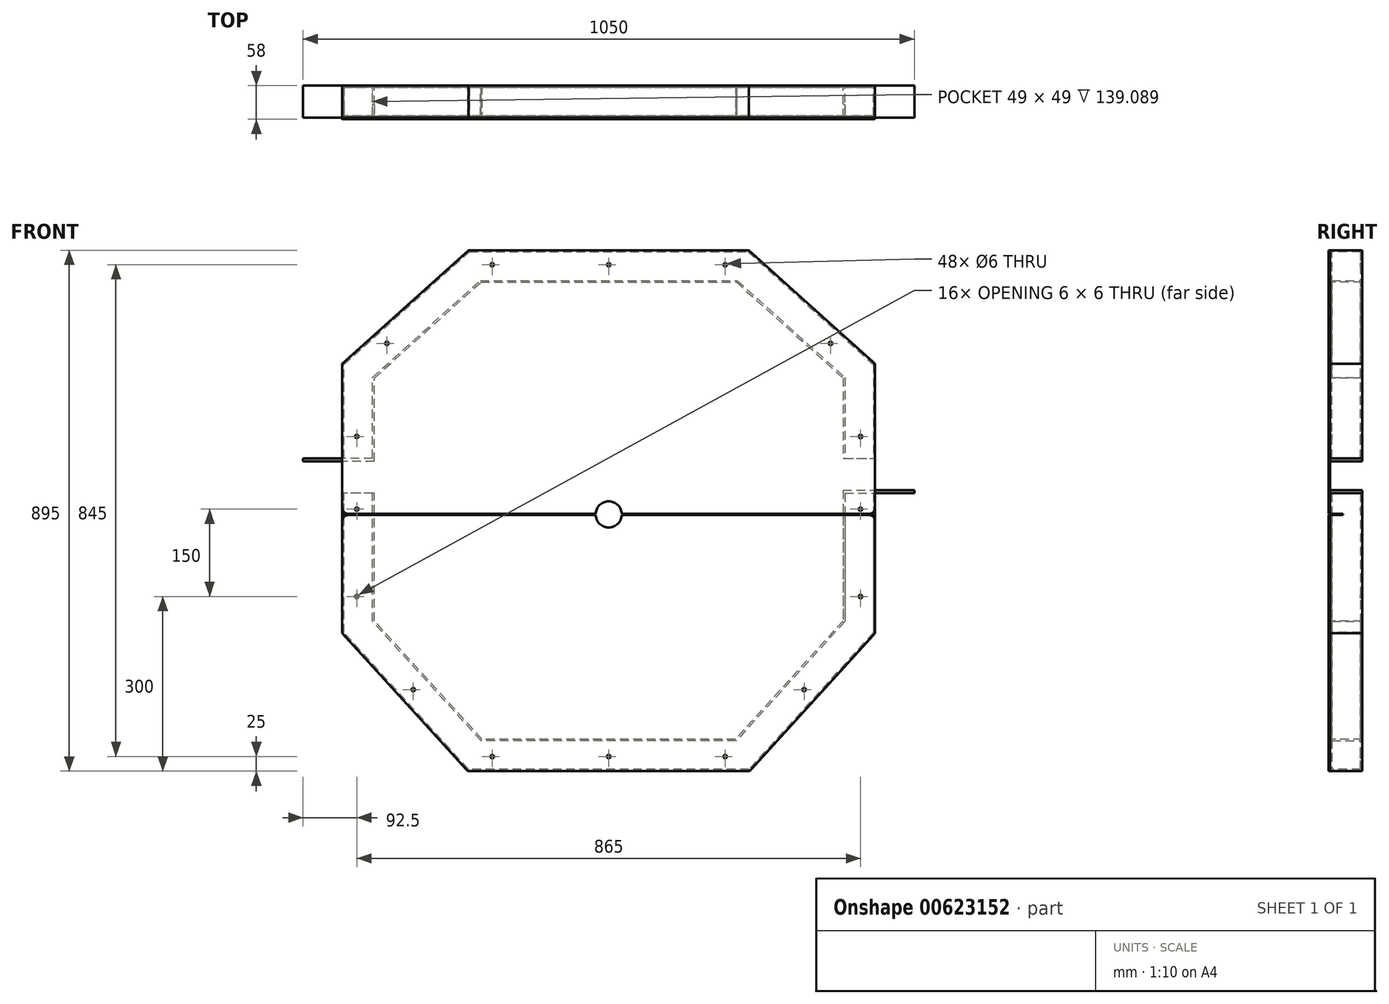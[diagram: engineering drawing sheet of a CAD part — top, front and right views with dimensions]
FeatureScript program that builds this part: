
annotation { "Feature Type Name" : "Feature", "Feature Type Description" : "" }
export const myFeature = defineFeature(function(context is Context, id is Id, definition is map)
    precondition{}
    {
        {
            var Q0;
            Q0=qCreatedBy(makeId("Front.planeOp"),FACE);
            var sketch = newSketch(context, id + "F0", { "sketchPlane" : qUnion([Q0])});
            skLineSegment(sketch, "E0", {"start": v(0, 0) * mm, "end": v(-430, 0) * mm, "construction": true});
            skLineSegment(sketch, "E1", {"start": v(0, 0) * mm, "end": v(430, 0) * mm, "construction": true});
            skPoint(sketch, "E2", {"position": v(0, -330) * mm});
            skLineSegment(sketch, "E3", {"start": v(-430, -330) * mm, "end": v(430, -330) * mm, "construction": true});
            skLineSegment(sketch, "E4", {"start": v(-430, -330) * mm, "end": v(-430, -180) * mm});
            skLineSegment(sketch, "E5", {"start": v(-430, -180) * mm, "end": v(-230, 0) * mm});
            skLineSegment(sketch, "E6", {"start": v(-230, 0) * mm, "end": v(0, 0) * mm});
            skLineSegment(sketch, "E7", {"start": v(0, 0) * mm, "end": v(230, 0) * mm});
            skLineSegment(sketch, "E8", {"start": v(430, -330) * mm, "end": v(430, -180) * mm});
            skLineSegment(sketch, "E9", {"start": v(430, -180) * mm, "end": v(230, 0) * mm});
            skSolve(sketch);
        }
        {
            var Q0;
            Q0=qCreatedBy(makeId("Top.planeOp"),FACE);
            cPlane(context, id + "F1", {"entities" : qUnion([Q0]), "cplaneType" : CPlaneType.OFFSET, "offset" : 330 * mm, "oppositeDirection" : true, "width" : 150 * mm, "height" : 150 * mm});
        }
        {
            var Q0;
            Q0=qCreatedBy(id+"F1.planeOp",FACE);
            var sketch = newSketch(context, id + "F2", { "sketchPlane" : qUnion([Q0])});
            skPoint(sketch, "E10", {"position": v(-430, 0) * mm});
            skLineSegment(sketch, "E11.bottom", {"start": v(-402.5, -27.5) * mm, "end": v(-457.5, -27.5) * mm});
            skLineSegment(sketch, "E11.top", {"start": v(-402.5, 27.5) * mm, "end": v(-457.5, 27.5) * mm});
            skLineSegment(sketch, "E11.left", {"start": v(-402.5, -27.5) * mm, "end": v(-402.5, 27.5) * mm});
            skLineSegment(sketch, "E11.right", {"start": v(-457.5, -27.5) * mm, "end": v(-457.5, 27.5) * mm});
            skLineSegment(sketch, "E12.bottom", {"start": v(-405.5, -24.5) * mm, "end": v(-454.5, -24.5) * mm});
            skLineSegment(sketch, "E12.top", {"start": v(-405.5, 24.5) * mm, "end": v(-454.5, 24.5) * mm});
            skLineSegment(sketch, "E12.left", {"start": v(-405.5, -24.5) * mm, "end": v(-405.5, 24.5) * mm});
            skLineSegment(sketch, "E12.right", {"start": v(-454.5, -24.5) * mm, "end": v(-454.5, 24.5) * mm});
            skSolve(sketch);
        }
        {
            var Q0;
            Q0=makeQuery(id+"F2.imprint","IMPRINT",FACE,{"disambiguationData":[TD([[makeQuery(id+"F2.imprint","IMPRINT",EDGE,{"derivedFrom":sQuery(id+"F2.wireOp",EDGE,"E11.bottom")}),-1.0]])]});
            var Q1;
            Q1=sQuery(id+"F0.wireOp",EDGE,"E4");
            var Q2;
            Q2=sQuery(id+"F0.wireOp",EDGE,"E5");
            var Q3;
            Q3=sQuery(id+"F0.wireOp",EDGE,"E6");
            var Q4;
            Q4=sQuery(id+"F0.wireOp",EDGE,"E7");
            var Q5;
            Q5=sQuery(id+"F0.wireOp",EDGE,"E9");
            var Q6;
            Q6=sQuery(id+"F0.wireOp",EDGE,"E8");
            sweep(context, id + "F3", {"profiles" : qUnion([Q0]), "path" : qUnion([Q1, Q2, Q3, Q4, Q5, Q6])});
        }
        {
            var Q0;
            Q0=makeQuery(id+"F3.opSweep","CAP_FACE",FACE,{"disambiguationData":[OSD([sQuery(id+"F0.wireOp",VERTEX,"E4.start"),sQuery(id+"F2.wireOp",EDGE,"E11.bottom"),sQuery(id+"F2.wireOp",EDGE,"E11.top"),sQuery(id+"F2.wireOp",EDGE,"E11.left"),sQuery(id+"F2.wireOp",EDGE,"E11.right"),sQuery(id+"F2.wireOp",EDGE,"E12.bottom"),sQuery(id+"F2.wireOp",EDGE,"E12.top"),sQuery(id+"F2.wireOp",EDGE,"E12.left"),sQuery(id+"F2.wireOp",EDGE,"E12.right")])],"isStart":true});
            var sketch = newSketch(context, id + "F4", { "sketchPlane" : qUnion([Q0])});
            skLineSegment(sketch, "E13.bottom", {"start": v(-402.5, 27.5) * mm, "end": v(-525, 27.5) * mm});
            skLineSegment(sketch, "E13.top", {"start": v(-402.5, -27.5) * mm, "end": v(-525, -27.5) * mm});
            skLineSegment(sketch, "E13.left", {"start": v(-402.5, 27.5) * mm, "end": v(-402.5, -27.5) * mm});
            skLineSegment(sketch, "E13.right", {"start": v(-525, 27.5) * mm, "end": v(-525, -27.5) * mm});
            skSolve(sketch);
        }
        {
            var Q0;
            Q0=qSketchRegion(id+"F4",true);
            extrude(context, id + "F5", {"entities" : qUnion([Q0]), "operationType" : NewBodyOperationType.ADD, "depth" : 5 * mm, "offsetDistance" : 25 * mm});
        }
        {
            var Q0;
            Q0=qCreatedBy(id+"F1.planeOp",FACE);
            cPlane(context, id + "F6", {"entities" : qUnion([Q0]), "cplaneType" : CPlaneType.OFFSET, "offset" : 60 * mm, "oppositeDirection" : true, "width" : 150 * mm, "height" : 150 * mm});
        }
        {
            var Q0;
            Q0=qCreatedBy(makeId("Front.planeOp"),FACE);
            var sketch = newSketch(context, id + "F7", { "sketchPlane" : qUnion([Q0])});
            skPoint(sketch, "E14", {"position": v(0, -390) * mm});
            skLineSegment(sketch, "E15", {"start": v(0, -390) * mm, "end": v(-430, -390) * mm, "construction": true});
            skLineSegment(sketch, "E16", {"start": v(0, -390) * mm, "end": v(430, -390) * mm, "construction": true});
            skLineSegment(sketch, "E17", {"start": v(0, -390) * mm, "end": v(0, -840) * mm, "construction": true});
            skLineSegment(sketch, "E18", {"start": v(-430, -390) * mm, "end": v(-430, -620) * mm});
            skLineSegment(sketch, "E19", {"start": v(430, -390) * mm, "end": v(430, -620) * mm});
            skLineSegment(sketch, "E20", {"start": v(0, -840) * mm, "end": v(-230, -840) * mm});
            skLineSegment(sketch, "E21", {"start": v(0, -840) * mm, "end": v(230, -840) * mm});
            skLineSegment(sketch, "E22", {"start": v(230, -840) * mm, "end": v(430, -620) * mm});
            skLineSegment(sketch, "E23", {"start": v(-430, -620) * mm, "end": v(-230, -840) * mm});
            skSolve(sketch);
        }
        {
            var Q0;
            Q0=qCreatedBy(id+"F6.planeOp",FACE);
            var sketch = newSketch(context, id + "F8", { "sketchPlane" : qUnion([Q0])});
            skPoint(sketch, "E24", {"position": v(430, 0) * mm});
            skLineSegment(sketch, "E25.bottom", {"start": v(402.5, -27.5) * mm, "end": v(457.5, -27.5) * mm});
            skLineSegment(sketch, "E25.top", {"start": v(402.5, 27.5) * mm, "end": v(457.5, 27.5) * mm});
            skLineSegment(sketch, "E25.left", {"start": v(402.5, -27.5) * mm, "end": v(402.5, 27.5) * mm});
            skLineSegment(sketch, "E25.right", {"start": v(457.5, -27.5) * mm, "end": v(457.5, 27.5) * mm});
            skLineSegment(sketch, "E26.bottom", {"start": v(405.5, -24.5) * mm, "end": v(454.5, -24.5) * mm});
            skLineSegment(sketch, "E26.top", {"start": v(405.5, 24.5) * mm, "end": v(454.5, 24.5) * mm});
            skLineSegment(sketch, "E26.left", {"start": v(405.5, -24.5) * mm, "end": v(405.5, 24.5) * mm});
            skLineSegment(sketch, "E26.right", {"start": v(454.5, -24.5) * mm, "end": v(454.5, 24.5) * mm});
            skSolve(sketch);
        }
        {
            var Q0;
            Q0=makeQuery(id+"F8.imprint","IMPRINT",FACE,{"disambiguationData":[TD([[makeQuery(id+"F8.imprint","IMPRINT",EDGE,{"derivedFrom":sQuery(id+"F8.wireOp",EDGE,"E25.bottom")}),1.0]])]});
            var Q1;
            Q1=sQuery(id+"F7.wireOp",EDGE,"E19");
            var Q2;
            Q2=sQuery(id+"F7.wireOp",EDGE,"E22");
            var Q3;
            Q3=sQuery(id+"F7.wireOp",EDGE,"E21");
            var Q4;
            Q4=sQuery(id+"F7.wireOp",EDGE,"E20");
            var Q5;
            Q5=sQuery(id+"F7.wireOp",EDGE,"E23");
            var Q6;
            Q6=sQuery(id+"F7.wireOp",EDGE,"E18");
            sweep(context, id + "F9", {"profiles" : qUnion([Q0]), "path" : qUnion([Q1, Q2, Q3, Q4, Q5, Q6])});
        }
        {
            var Q0;
            Q0=makeQuery(id+"F9.opSweep","CAP_FACE",FACE,{"disambiguationData":[OSD([sQuery(id+"F7.wireOp",VERTEX,"E19.start"),sQuery(id+"F8.wireOp",EDGE,"E25.bottom"),sQuery(id+"F8.wireOp",EDGE,"E25.top"),sQuery(id+"F8.wireOp",EDGE,"E25.left"),sQuery(id+"F8.wireOp",EDGE,"E25.right"),sQuery(id+"F8.wireOp",EDGE,"E26.bottom"),sQuery(id+"F8.wireOp",EDGE,"E26.top"),sQuery(id+"F8.wireOp",EDGE,"E26.left"),sQuery(id+"F8.wireOp",EDGE,"E26.right")])],"isStart":true});
            var sketch = newSketch(context, id + "F10", { "sketchPlane" : qUnion([Q0])});
            skLineSegment(sketch, "E27.bottom", {"start": v(402.5, -27.5) * mm, "end": v(525, -27.5) * mm});
            skLineSegment(sketch, "E27.top", {"start": v(402.5, 27.5) * mm, "end": v(525, 27.5) * mm});
            skLineSegment(sketch, "E27.left", {"start": v(402.5, -27.5) * mm, "end": v(402.5, 27.5) * mm});
            skLineSegment(sketch, "E27.right", {"start": v(525, -27.5) * mm, "end": v(525, 27.5) * mm});
            skSolve(sketch);
        }
        {
            var Q0;
            Q0=qSketchRegion(id+"F10",true);
            extrude(context, id + "F11", {"entities" : qUnion([Q0]), "operationType" : NewBodyOperationType.ADD, "depth" : 5 * mm, "offsetDistance" : 25 * mm});
        }
        {
            var Q0;
            {var subQ0=sQuery(id+"F4.wireOp",EDGE,"E13.bottom");Q0=makeQuery(id+"FolUU5aMUaDlA69_1.1.F5.boolean.opBoolean","MERGE",FACE,{"derivedFrom":[makeQuery(id+"F5.boolean.opBoolean","MERGE",FACE,{"derivedFrom":[makeQuery(id+"F3.opSweep","SWEPT_FACE",FACE,{"disambiguationData":[OSD([sQuery(id+"F0.wireOp",EDGE,"E4"),sQuery(id+"F2.wireOp",EDGE,"E11.bottom")])]}),makeQuery(id+"F5.opExtrude","SWEPT_FACE",FACE,{"disambiguationData":[OSD([subQ0])]})]}),makeQuery(id+"FolUU5aMUaDlA69_1.1.F5.opExtrude","SWEPT_FACE",FACE,{"disambiguationData":[OSD([subQ0])]})]});}
            var sketch = newSketch(context, id + "F12", { "sketchPlane" : qUnion([Q0])});
            skLineSegment(sketch, "E28.0", {"start": v(-457.5, -167.75) * mm, "end": v(-240.55, 27.5) * mm});
            skLineSegment(sketch, "E29.0", {"start": v(-240.55, 27.5) * mm, "end": v(240.55, 27.5) * mm});
            skLineSegment(sketch, "E30.0", {"start": v(240.55, 27.5) * mm, "end": v(457.5, -167.75) * mm});
            skLineSegment(sketch, "E31.0", {"start": v(457.5, -630.63) * mm, "end": v(242.17, -867.5) * mm});
            skLineSegment(sketch, "E32.0", {"start": v(-242.17, -867.5) * mm, "end": v(-457.5, -630.63) * mm});
            skLineSegment(sketch, "E33.0", {"start": v(242.17, -867.5) * mm, "end": v(-242.17, -867.5) * mm});
            skLineSegment(sketch, "E34", {"start": v(-457.5, -167.75) * mm, "end": v(-457.5, -630.63) * mm});
            skLineSegment(sketch, "E35", {"start": v(457.5, -167.75) * mm, "end": v(457.5, -630.63) * mm});
            skSolve(sketch);
        }
        {
            var Q0;
            Q0=qSketchRegion(id+"F12",true);
            extrude(context, id + "F13", {"entities" : qUnion([Q0]), "depth" : 3 * mm, "offsetDistance" : 25 * mm});
        }
        {
            var Q0;
            Q0=makeQuery(id+"F13.opExtrude","CAP_FACE",FACE,{"disambiguationData":[OSD([sQuery(id+"F12.wireOp",EDGE,"E28.0"),sQuery(id+"F12.wireOp",EDGE,"E29.0"),sQuery(id+"F12.wireOp",EDGE,"E30.0"),sQuery(id+"F12.wireOp",EDGE,"E31.0"),sQuery(id+"F12.wireOp",EDGE,"E32.0"),sQuery(id+"F12.wireOp",EDGE,"E33.0"),sQuery(id+"F12.wireOp",EDGE,"E34"),sQuery(id+"F12.wireOp",EDGE,"E35")])],"isStart":false});
            var sketch = newSketch(context, id + "F14", { "sketchPlane" : qUnion([Q0])});
            skPoint(sketch, "E36", {"position": v(0, -426.5) * mm});
            skPoint(sketch, "E36.positionSnap0", {"position": v(0, -867.5) * mm});
            skCircle(sketch, "E37", {"center": v(0, -426.5) * mm, "radius": 22.5 * mm});
            skLineSegment(sketch, "E38.bottom", {"start": v(475, -425.5) * mm, "end": v(-475, -425.5) * mm});
            skLineSegment(sketch, "E38.top", {"start": v(475, -427.5) * mm, "end": v(-475, -427.5) * mm});
            skLineSegment(sketch, "E38.left", {"start": v(475, -425.5) * mm, "end": v(475, -427.5) * mm});
            skLineSegment(sketch, "E38.right", {"start": v(-475, -425.5) * mm, "end": v(-475, -427.5) * mm});
            skSolve(sketch);
        }
        {
            var Q0;
            Q0=qSketchRegion(id+"F14",true);
            extrude(context, id + "F15", {"entities" : qUnion([Q0]), "operationType" : NewBodyOperationType.REMOVE, "oppositeDirection" : true, "depth" : 25 * mm, "offsetDistance" : 25 * mm});
        }
        {
            var Q0;
            {var subQ0=sQuery(id+"F12.wireOp",EDGE,"E30.0");var subQ1=sQuery(id+"F12.wireOp",EDGE,"E34");var subQ2=sQuery(id+"F12.wireOp",EDGE,"E29.0");var subQ3=sQuery(id+"F12.wireOp",EDGE,"E28.0");var subQ4=sQuery(id+"F12.wireOp",EDGE,"E35");Q0=makeQuery(id+"F15.boolean.opBoolean","SPLIT",FACE,{"disambiguationData":[TD([makeQuery(id+"F13.opExtrude","SWEPT_FACE",FACE,{"disambiguationData":[OSD([subQ3])]})])],"derivedFrom":makeQuery(id+"F13.opExtrude","CAP_FACE",FACE,{"disambiguationData":[OSD([subQ3,subQ2,subQ0,sQuery(id+"F12.wireOp",EDGE,"E31.0"),sQuery(id+"F12.wireOp",EDGE,"E32.0"),sQuery(id+"F12.wireOp",EDGE,"E33.0"),subQ1,subQ4])],"isStart":false})});}
            var sketch = newSketch(context, id + "F16", { "sketchPlane" : qUnion([Q0])});
            skPoint(sketch, "E39", {"position": v(-200, 2.5) * mm});
            skPoint(sketch, "E40", {"position": v(200, 2.5) * mm});
            skPoint(sketch, "E41", {"position": v(-380.96, -132.5) * mm});
            skPoint(sketch, "E42", {"position": v(380.96, -132.5) * mm});
            skPoint(sketch, "E43", {"position": v(-432.5, -292.5) * mm});
            skPoint(sketch, "E44", {"position": v(432.5, -292.5) * mm});
            skPoint(sketch, "E45", {"position": v(-432.5, -417.5) * mm});
            skPoint(sketch, "E46", {"position": v(432.5, -417.5) * mm});
            skPoint(sketch, "E47", {"position": v(-432.5, -567.5) * mm});
            skPoint(sketch, "E48", {"position": v(432.5, -567.5) * mm});
            skPoint(sketch, "E49", {"position": v(0, 2.5) * mm});
            skPoint(sketch, "E49.positionSnap0", {"position": v(0, 27.5) * mm});
            skPoint(sketch, "E50", {"position": v(0, -842.5) * mm});
            skPoint(sketch, "E51", {"position": v(-200, -842.5) * mm});
            skPoint(sketch, "E52", {"position": v(200, -842.5) * mm});
            skPoint(sketch, "E53", {"position": v(-335.65, -727.5) * mm});
            skPoint(sketch, "E54", {"position": v(335.65, -727.5) * mm});
            skCircle(sketch, "E55", {"center": v(-200, 2.5) * mm, "radius": 3 * mm});
            skCircle(sketch, "E56", {"center": v(0, 2.5) * mm, "radius": 3 * mm});
            skCircle(sketch, "E57", {"center": v(200, 2.5) * mm, "radius": 3 * mm});
            skCircle(sketch, "E58", {"center": v(380.96, -132.5) * mm, "radius": 3 * mm});
            skCircle(sketch, "E59", {"center": v(-380.96, -132.5) * mm, "radius": 3 * mm});
            skCircle(sketch, "E60", {"center": v(-432.5, -292.5) * mm, "radius": 3 * mm});
            skCircle(sketch, "E61", {"center": v(432.5, -292.5) * mm, "radius": 3 * mm});
            skCircle(sketch, "E62", {"center": v(432.5, -417.5) * mm, "radius": 3 * mm});
            skCircle(sketch, "E63", {"center": v(432.5, -567.5) * mm, "radius": 3 * mm});
            skCircle(sketch, "E64", {"center": v(335.65, -727.5) * mm, "radius": 3 * mm});
            skCircle(sketch, "E65", {"center": v(200, -842.5) * mm, "radius": 3 * mm});
            skCircle(sketch, "E66", {"center": v(0, -842.5) * mm, "radius": 3 * mm});
            skCircle(sketch, "E67", {"center": v(-200, -842.5) * mm, "radius": 3 * mm});
            skCircle(sketch, "E68", {"center": v(-335.65, -727.5) * mm, "radius": 3 * mm});
            skCircle(sketch, "E69", {"center": v(-432.5, -567.5) * mm, "radius": 3 * mm});
            skCircle(sketch, "E70", {"center": v(-432.5, -417.5) * mm, "radius": 3 * mm});
            skSolve(sketch);
        }
        {
            var Q0;
            Q0=qSketchRegion(id+"F16",true);
            extrude(context, id + "F17", {"entities" : qUnion([Q0]), "operationType" : NewBodyOperationType.REMOVE, "oppositeDirection" : true, "depth" : 60 * mm, "offsetDistance" : 25 * mm});
        }
        {
            var Q0;
            Q0=makeQuery(id+"F13.opExtrude","SWEPT_EDGE",EDGE,{"disambiguationData":[OSD([sQuery(id+"F12.wireOp",EDGE,"E30.0"),sQuery(id+"F12.wireOp",EDGE,"E35")])]});
            var Q1;
            {var subQ0=sQuery(id+"F14.wireOp",EDGE,"E38.bottom");var subQ1=sQuery(id+"F12.wireOp",EDGE,"E35");Q1=makeQuery(id+"F15.boolean.opBoolean","INTERSECT",EDGE,{"derivedFrom":[makeQuery(id+"F13.opExtrude","SWEPT_FACE",FACE,{"disambiguationData":[OSD([subQ1])]}),makeQuery(id+"F15.opExtrude","SWEPT_FACE",FACE,{"disambiguationData":[OSD([subQ0]),TDD([makeQuery(id+"F14.imprint","IMPRINT",EDGE,{"disambiguationData":[TD([[makeQuery(id+"F14.imprint","INTERSECT",VERTEX,{"derivedFrom":[subQ0,sQuery(id+"F14.wireOp",EDGE,"E38.left")]}),-1.0]])],"derivedFrom":subQ0}),makeQuery(id+"F14.imprint","IMPRINT",EDGE,{"disambiguationData":[TD([[makeQuery(id+"F14.imprint","INTERSECT",VERTEX,{"disambiguationData":[OD(1.0)],"derivedFrom":[sQuery(id+"F14.wireOp",EDGE,"E37"),subQ0]}),1.0]])],"derivedFrom":subQ0})])]})]});}
            var Q2;
            {var subQ0=sQuery(id+"F14.wireOp",EDGE,"E38.top");var subQ1=sQuery(id+"F12.wireOp",EDGE,"E35");Q2=makeQuery(id+"F15.boolean.opBoolean","INTERSECT",EDGE,{"derivedFrom":[makeQuery(id+"F13.opExtrude","SWEPT_FACE",FACE,{"disambiguationData":[OSD([subQ1])]}),makeQuery(id+"F15.opExtrude","SWEPT_FACE",FACE,{"disambiguationData":[OSD([subQ0]),TDD([makeQuery(id+"F14.imprint","IMPRINT",EDGE,{"disambiguationData":[TD([[makeQuery(id+"F14.imprint","INTERSECT",VERTEX,{"derivedFrom":[subQ0,sQuery(id+"F14.wireOp",EDGE,"E38.left")]}),-1.0]])],"derivedFrom":subQ0}),makeQuery(id+"F14.imprint","IMPRINT",EDGE,{"disambiguationData":[TD([[makeQuery(id+"F14.imprint","INTERSECT",VERTEX,{"disambiguationData":[OD(1.0)],"derivedFrom":[sQuery(id+"F14.wireOp",EDGE,"E37"),subQ0]}),1.0]])],"derivedFrom":subQ0})])]})]});}
            var Q3;
            Q3=makeQuery(id+"F13.opExtrude","SWEPT_EDGE",EDGE,{"disambiguationData":[OSD([sQuery(id+"F12.wireOp",EDGE,"E31.0"),sQuery(id+"F12.wireOp",EDGE,"E35")])]});
            var Q4;
            Q4=makeQuery(id+"F13.opExtrude","SWEPT_EDGE",EDGE,{"disambiguationData":[OSD([sQuery(id+"F12.wireOp",EDGE,"E31.0"),sQuery(id+"F12.wireOp",EDGE,"E33.0")])]});
            var Q5;
            Q5=makeQuery(id+"F13.opExtrude","SWEPT_EDGE",EDGE,{"disambiguationData":[OSD([sQuery(id+"F12.wireOp",EDGE,"E32.0"),sQuery(id+"F12.wireOp",EDGE,"E33.0")])]});
            var Q6;
            Q6=makeQuery(id+"F13.opExtrude","SWEPT_EDGE",EDGE,{"disambiguationData":[OSD([sQuery(id+"F12.wireOp",EDGE,"E32.0"),sQuery(id+"F12.wireOp",EDGE,"E34")])]});
            var Q7;
            {var subQ0=sQuery(id+"F14.wireOp",EDGE,"E38.bottom");var subQ1=sQuery(id+"F12.wireOp",EDGE,"E34");Q7=makeQuery(id+"F15.boolean.opBoolean","INTERSECT",EDGE,{"derivedFrom":[makeQuery(id+"F13.opExtrude","SWEPT_FACE",FACE,{"disambiguationData":[OSD([subQ1])]}),makeQuery(id+"F15.opExtrude","SWEPT_FACE",FACE,{"disambiguationData":[OSD([subQ0]),TDD([makeQuery(id+"F14.imprint","IMPRINT",EDGE,{"disambiguationData":[TD([[makeQuery(id+"F14.imprint","INTERSECT",VERTEX,{"disambiguationData":[OD(0.0)],"derivedFrom":[sQuery(id+"F14.wireOp",EDGE,"E37"),subQ0]}),-1.0]])],"derivedFrom":subQ0}),makeQuery(id+"F14.imprint","IMPRINT",EDGE,{"disambiguationData":[TD([[makeQuery(id+"F14.imprint","INTERSECT",VERTEX,{"derivedFrom":[subQ0,sQuery(id+"F14.wireOp",EDGE,"E38.right")]}),1.0]])],"derivedFrom":subQ0})])]})]});}
            var Q8;
            {var subQ0=sQuery(id+"F14.wireOp",EDGE,"E38.top");var subQ1=sQuery(id+"F12.wireOp",EDGE,"E34");Q8=makeQuery(id+"F15.boolean.opBoolean","INTERSECT",EDGE,{"derivedFrom":[makeQuery(id+"F13.opExtrude","SWEPT_FACE",FACE,{"disambiguationData":[OSD([subQ1])]}),makeQuery(id+"F15.opExtrude","SWEPT_FACE",FACE,{"disambiguationData":[OSD([subQ0]),TDD([makeQuery(id+"F14.imprint","IMPRINT",EDGE,{"disambiguationData":[TD([[makeQuery(id+"F14.imprint","INTERSECT",VERTEX,{"disambiguationData":[OD(0.0)],"derivedFrom":[sQuery(id+"F14.wireOp",EDGE,"E37"),subQ0]}),-1.0]])],"derivedFrom":subQ0}),makeQuery(id+"F14.imprint","IMPRINT",EDGE,{"disambiguationData":[TD([[makeQuery(id+"F14.imprint","INTERSECT",VERTEX,{"derivedFrom":[subQ0,sQuery(id+"F14.wireOp",EDGE,"E38.right")]}),1.0]])],"derivedFrom":subQ0})])]})]});}
            var Q9;
            Q9=makeQuery(id+"F13.opExtrude","SWEPT_EDGE",EDGE,{"disambiguationData":[OSD([sQuery(id+"F12.wireOp",EDGE,"E28.0"),sQuery(id+"F12.wireOp",EDGE,"E34")])]});
            var Q10;
            Q10=makeQuery(id+"F13.opExtrude","SWEPT_EDGE",EDGE,{"disambiguationData":[OSD([sQuery(id+"F12.wireOp",EDGE,"E28.0"),sQuery(id+"F12.wireOp",EDGE,"E29.0")])]});
            var Q11;
            Q11=makeQuery(id+"F13.opExtrude","SWEPT_EDGE",EDGE,{"disambiguationData":[OSD([sQuery(id+"F12.wireOp",EDGE,"E29.0"),sQuery(id+"F12.wireOp",EDGE,"E30.0")])]});
            fillet(context, id + "F18", {"entities" : qUnion([Q0, Q1, Q2, Q3, Q4, Q5, Q6, Q7, Q8, Q9, Q10, Q11]), "radius" : 10 * mm, "tangentPropagation" : true, "allowEdgeOverflow" : false});
        }
    });
